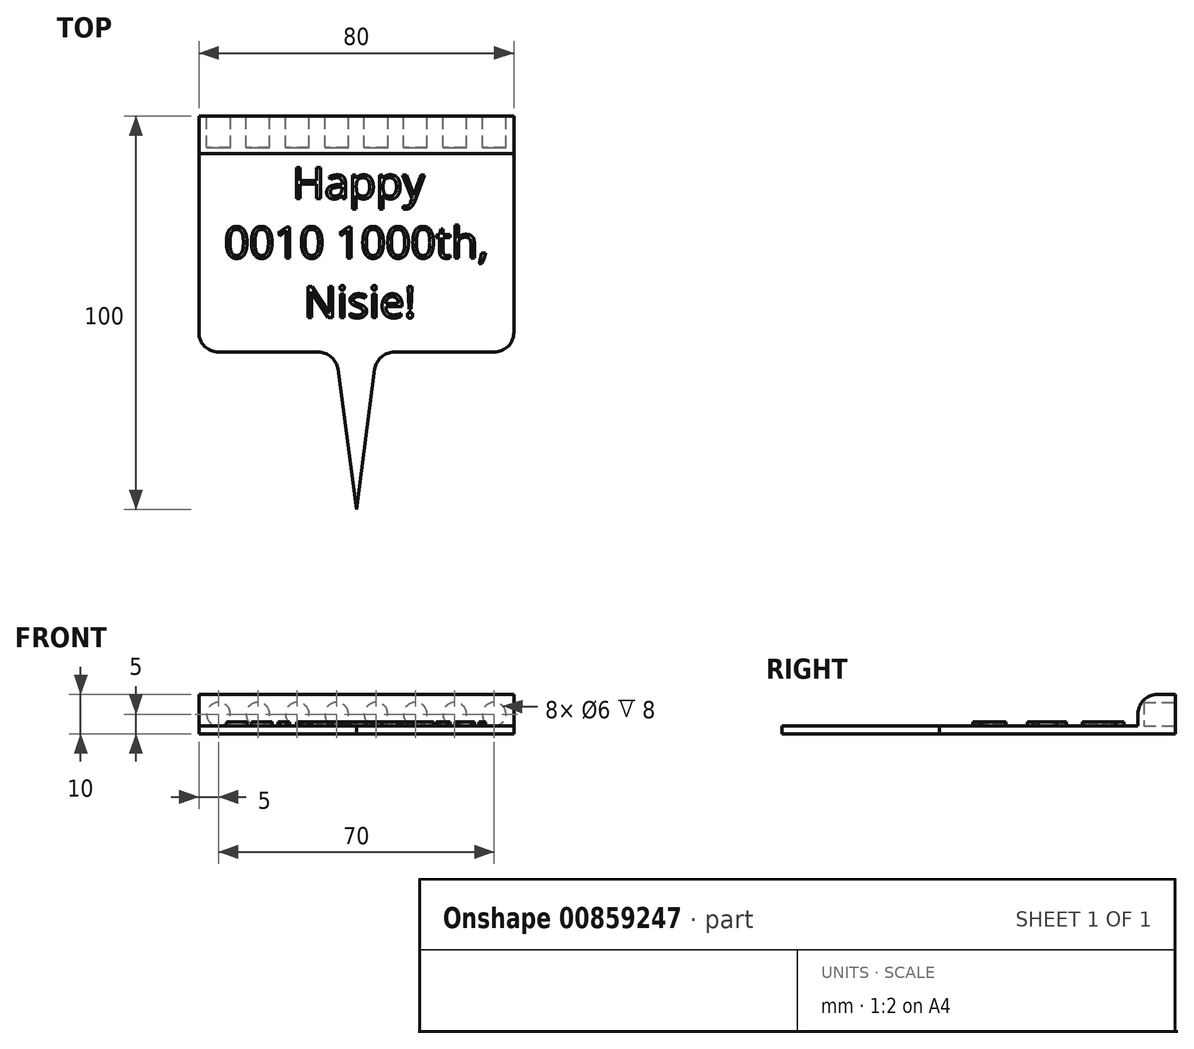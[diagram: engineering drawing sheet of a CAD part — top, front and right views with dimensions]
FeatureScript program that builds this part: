
annotation { "Feature Type Name" : "Feature", "Feature Type Description" : "" }
export const myFeature = defineFeature(function(context is Context, id is Id, definition is map)
    precondition{}
    {
        {
            var Q0;
            Q0=qCreatedBy(makeId("Top.planeOp"),FACE);
            var sketch = newSketch(context, id + "F0", { "sketchPlane" : qUnion([Q0])});
            skLineSegment(sketch, "E0.bottom", {"start": v(-40, 0) * mm, "end": v(40, 0) * mm});
            skLineSegment(sketch, "E0.top", {"start": v(-40, 60) * mm, "end": v(40, 60) * mm});
            skLineSegment(sketch, "E0.left", {"start": v(-40, 0) * mm, "end": v(-40, 60) * mm});
            skLineSegment(sketch, "E0.right", {"start": v(40, 0) * mm, "end": v(40, 60) * mm});
            skLineSegment(sketch, "E1", {"start": v(-5.27, 0) * mm, "end": v(0, -40) * mm});
            skLineSegment(sketch, "E2", {"start": v(0, -40) * mm, "end": v(5.27, 0) * mm});
            skSolve(sketch);
        }
        {
            var Q0;
            Q0 = qSketchRegion(id + "F0", true);
            extrude(context, id + "F1", {"entities" : qUnion([Q0]), "depth" : 2 * mm, "offsetDistance" : 25 * mm});
        }
        {
            var Q0;
            Q0=makeQuery(id+"F1.opExtrude","CAP_FACE",FACE,{"disambiguationData":[OSD([sQuery(id+"F0.wireOp",EDGE,"E0.bottom"),sQuery(id+"F0.wireOp",EDGE,"E0.top"),sQuery(id+"F0.wireOp",EDGE,"E0.left"),sQuery(id+"F0.wireOp",EDGE,"E0.right")])],"isStart":false});
            var sketch = newSketch(context, id + "F2", { "sketchPlane" : qUnion([Q0])});
            skText(sketch, "E3", { "text": "      Happy \n0010 1000th,\n       Nisie!", "fontName": "OpenSans-Regular.ttf"});
            skLineSegment(sketch, "E4", {"start": v(0, 60) * mm, "end": v(0, 47) * mm, "construction": true});
            const initialGuessF2  = {"E3": [-0.03357, 0.039, 1, 0, 0.008]};
            skSetInitialGuess(sketch, initialGuessF2);
            skSolve(sketch);
        }
        {
            var Q0;
            Q0 = qSketchRegion(id + "F2", true);
            extrude(context, id + "F3", {"entities" : qUnion([Q0]), "operationType" : NewBodyOperationType.ADD, "depth" : 1 * mm, "offsetDistance" : 25 * mm});
        }
        {
            var Q0;
            {var subQ0=sQuery(id+"F0.wireOp",EDGE,"E0.left");var subQ1=sQuery(id+"F0.wireOp",EDGE,"E0.bottom");var subQ2=sQuery(id+"F0.wireOp",EDGE,"E0.right");var subQ3=sQuery(id+"F0.wireOp",EDGE,"E0.top");Q0=makeQuery(id+"F3.boolean.opBoolean","SPLIT",FACE,{"disambiguationData":[TD([makeQuery(id+"F1.opExtrude","SWEPT_FACE",FACE,{"disambiguationData":[OSD([subQ1])]})])],"derivedFrom":makeQuery(id+"F1.opExtrude","CAP_FACE",FACE,{"disambiguationData":[OSD([subQ1,subQ3,subQ0,subQ2])],"isStart":false})});}
            var sketch = newSketch(context, id + "F4", { "sketchPlane" : qUnion([Q0])});
            skLineSegment(sketch, "E5.bottom", {"start": v(-40, 50.45) * mm, "end": v(40, 50.45) * mm});
            skLineSegment(sketch, "E5.top", {"start": v(-40, 60) * mm, "end": v(40, 60) * mm});
            skLineSegment(sketch, "E5.left", {"start": v(-40, 50.45) * mm, "end": v(-40, 60) * mm});
            skLineSegment(sketch, "E5.right", {"start": v(40, 50.45) * mm, "end": v(40, 60) * mm});
            skSolve(sketch);
        }
        {
            var Q0;
            Q0 = qSketchRegion(id + "F4", true);
            extrude(context, id + "F5", {"entities" : qUnion([Q0]), "operationType" : NewBodyOperationType.ADD, "depth" : 8 * mm, "offsetDistance" : 25 * mm});
        }
        {
            var Q0;
            Q0=makeQuery(id+"F5.boolean.opBoolean","MERGE",FACE,{"derivedFrom":[makeQuery(id+"F1.opExtrude","SWEPT_FACE",FACE,{"disambiguationData":[OSD([sQuery(id+"F0.wireOp",EDGE,"E0.top")])]}),makeQuery(id+"F5.opExtrude","SWEPT_FACE",FACE,{"disambiguationData":[OSD([sQuery(id+"F4.wireOp",EDGE,"E5.top")])]})]});
            var sketch = newSketch(context, id + "F6", { "sketchPlane" : qUnion([Q0])});
            skCircle(sketch, "E6", {"center": v(35, 5) * mm, "radius": 3 * mm});
            skLineSegment(sketch, "E7", {"start": v(35, 10) * mm, "end": v(35, 5) * mm, "construction": true});
            skLineSegment(sketch, "E8", {"start": v(40, 5) * mm, "end": v(35, 5) * mm, "construction": true});
            skLineSegment(sketch, "E9", {"start": v(35, 5) * mm, "end": v(35, 0) * mm, "construction": true});
            skCircle(sketch, "E10.1.0.0", {"center": v(25, 5) * mm, "radius": 3 * mm});
            skCircle(sketch, "E10.2.0.0", {"center": v(15, 5) * mm, "radius": 3 * mm});
            skCircle(sketch, "E10.3.0.0", {"center": v(5, 5) * mm, "radius": 3 * mm});
            skCircle(sketch, "E10.4.0.0", {"center": v(-5, 5) * mm, "radius": 3 * mm});
            skCircle(sketch, "E10.5.0.0", {"center": v(-15, 5) * mm, "radius": 3 * mm});
            skCircle(sketch, "E10.6.0.0", {"center": v(-25, 5) * mm, "radius": 3 * mm});
            skCircle(sketch, "E10.7.0.0", {"center": v(-35, 5) * mm, "radius": 3 * mm});
            skLineSegment(sketch, "E10.direction1", {"start": v(35, 5) * mm, "end": v(25, 5) * mm, "construction": true});
            skSolve(sketch);
        }
        {
            var Q0;
            Q0 = qSketchRegion(id + "F6", true);
            extrude(context, id + "F7", {"entities" : qUnion([Q0]), "operationType" : NewBodyOperationType.REMOVE, "oppositeDirection" : true, "depth" : 8 * mm, "offsetDistance" : 25 * mm});
        }
        {
            var Q0;
            Q0=makeQuery(id+"F5.opExtrude","CAP_EDGE",EDGE,{"disambiguationData":[OSD([sQuery(id+"F4.wireOp",EDGE,"E5.bottom")])],"isStart":false});
            var Q1;
            Q1=makeQuery(id+"F1.opExtrude","SWEPT_EDGE",EDGE,{"disambiguationData":[OSD([sQuery(id+"F0.wireOp",EDGE,"E0.bottom"),sQuery(id+"F0.wireOp",EDGE,"E0.left")])]});
            var Q2;
            Q2=makeQuery(id+"F1.opExtrude","SWEPT_EDGE",EDGE,{"disambiguationData":[OSD([sQuery(id+"F0.wireOp",EDGE,"E0.bottom"),sQuery(id+"F0.wireOp",EDGE,"E0.right")])]});
            var Q3;
            Q3=makeQuery(id+"F1.opExtrude","SWEPT_EDGE",EDGE,{"disambiguationData":[OSD([sQuery(id+"F0.wireOp",EDGE,"E0.bottom"),sQuery(id+"F0.wireOp",EDGE,"E2")])]});
            var Q4;
            Q4=makeQuery(id+"F1.opExtrude","SWEPT_EDGE",EDGE,{"disambiguationData":[OSD([sQuery(id+"F0.wireOp",EDGE,"E0.bottom"),sQuery(id+"F0.wireOp",EDGE,"E1")])]});
            fillet(context, id + "F8", {"entities" : qUnion([Q0, Q1, Q2, Q3, Q4]), "radius" : 5 * mm, "tangentPropagation" : true, "allowEdgeOverflow" : false});
        }
    });
